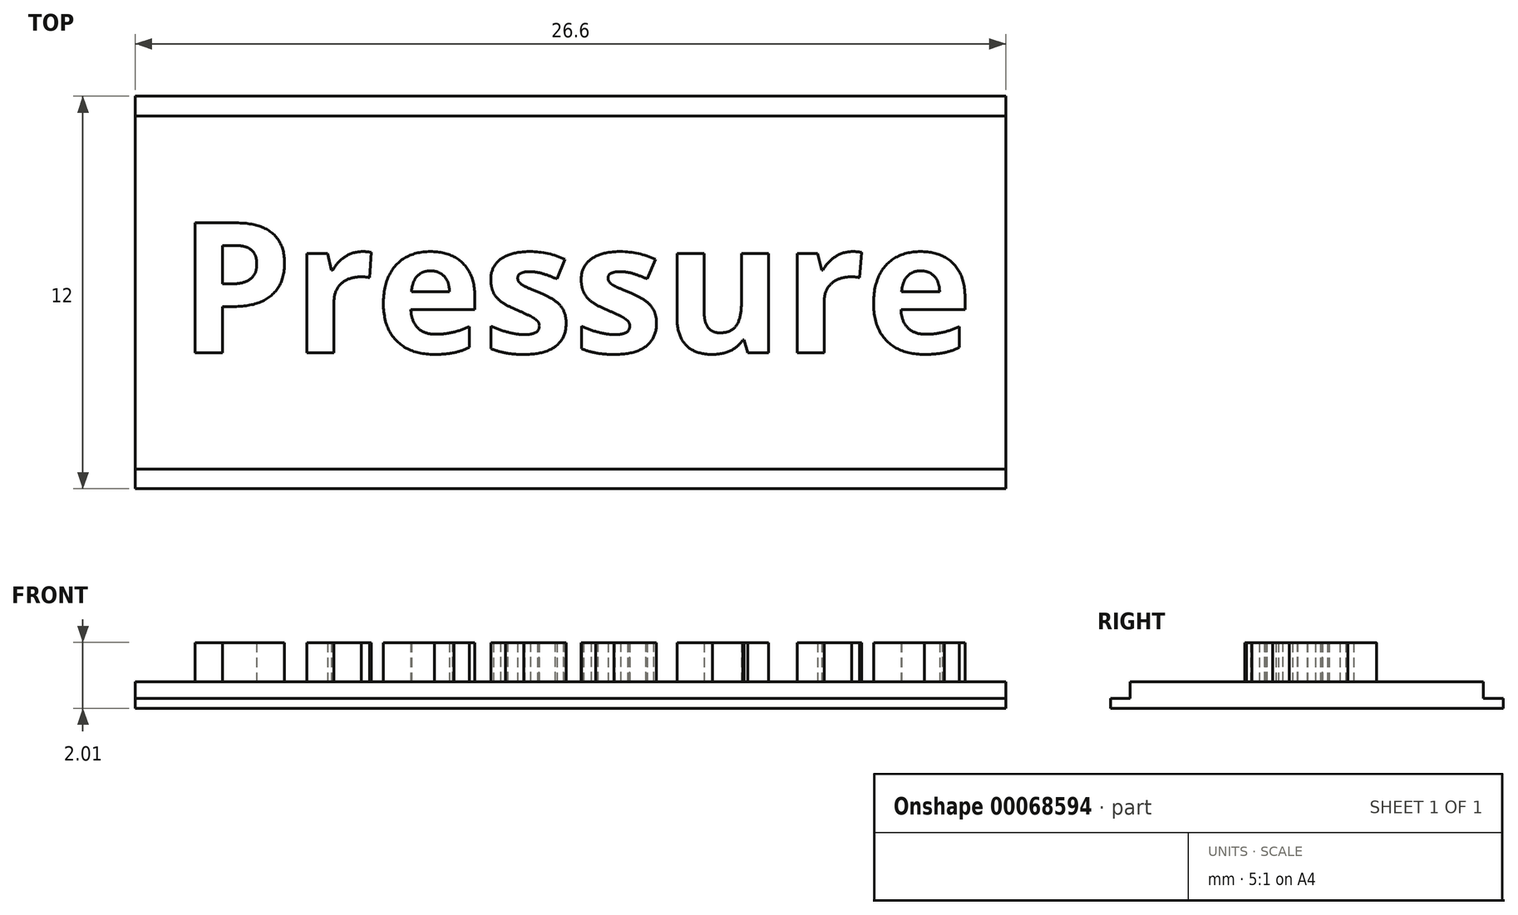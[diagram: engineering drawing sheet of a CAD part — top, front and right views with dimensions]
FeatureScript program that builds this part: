
annotation { "Feature Type Name" : "Feature", "Feature Type Description" : "" }
export const myFeature = defineFeature(function(context is Context, id is Id, definition is map)
    precondition{}
    {
        {
            var Q0;
            Q0=qCreatedBy(makeId("Right.planeOp"),FACE);
            var sketch = newSketch(context, id + "F0", { "sketchPlane" : qUnion([Q0])});
            skLineSegment(sketch, "E0.rect.bottom", {"start": v(6, -0.15) * mm, "end": v(-6, -0.15) * mm});
            skLineSegment(sketch, "E0.rect.left", {"start": v(6, -0.15) * mm, "end": v(6, 0.15) * mm});
            skLineSegment(sketch, "E0.rect.right", {"start": v(-6, -0.15) * mm, "end": v(-6, 0.15) * mm});
            skPoint(sketch, "E0.rect.middle", {"position": v(0, 0) * mm});
            skLineSegment(sketch, "E1.rect.bottom", {"start": v(5.4, 0.66) * mm, "end": v(-5.4, 0.66) * mm});
            skLineSegment(sketch, "E1.rect.left", {"start": v(5.4, 0.66) * mm, "end": v(5.4, 0.15) * mm});
            skLineSegment(sketch, "E2", {"start": v(6, 0.15) * mm, "end": v(5.4, 0.15) * mm});
            skLineSegment(sketch, "E3", {"start": v(-5.4, 0.66) * mm, "end": v(-5.4, 0.15) * mm});
            skLineSegment(sketch, "E4", {"start": v(-5.4, 0.15) * mm, "end": v(-6, 0.15) * mm});
            skSolve(sketch);
        }
        {
            var Q0;
            Q0 = qSketchRegion(id + "F0", true);
            extrude(context, id + "F1", {"entities" : qUnion([Q0]), "endBound" : BoundingType.SYMMETRIC, "depth" : 26.6 * mm});
        }
        {
            var Q0;
            Q0=makeQuery(id+"F1.opExtrude","SWEPT_FACE",FACE,{"disambiguationData":[OSD([sQuery(id+"F0.wireOp",EDGE,"E1.rect.bottom")])]});
            var sketch = newSketch(context, id + "F2", { "sketchPlane" : qUnion([Q0])});
            skText(sketch, "E5", { "text": "Pressure", "fontName": "OpenSans-Bold.ttf"});
            const initialGuessF2  = {"E5": [-0.01198, -0.00184, 1, 0, 0.004]};
            skSetInitialGuess(sketch, initialGuessF2);
            skSolve(sketch);
        }
        {
            var Q0;
            Q0 = qSketchRegion(id + "F2", true);
            extrude(context, id + "F3", {"entities" : qUnion([Q0]), "operationType" : NewBodyOperationType.ADD, "depth" : 1.2 * mm});
        }
    });
